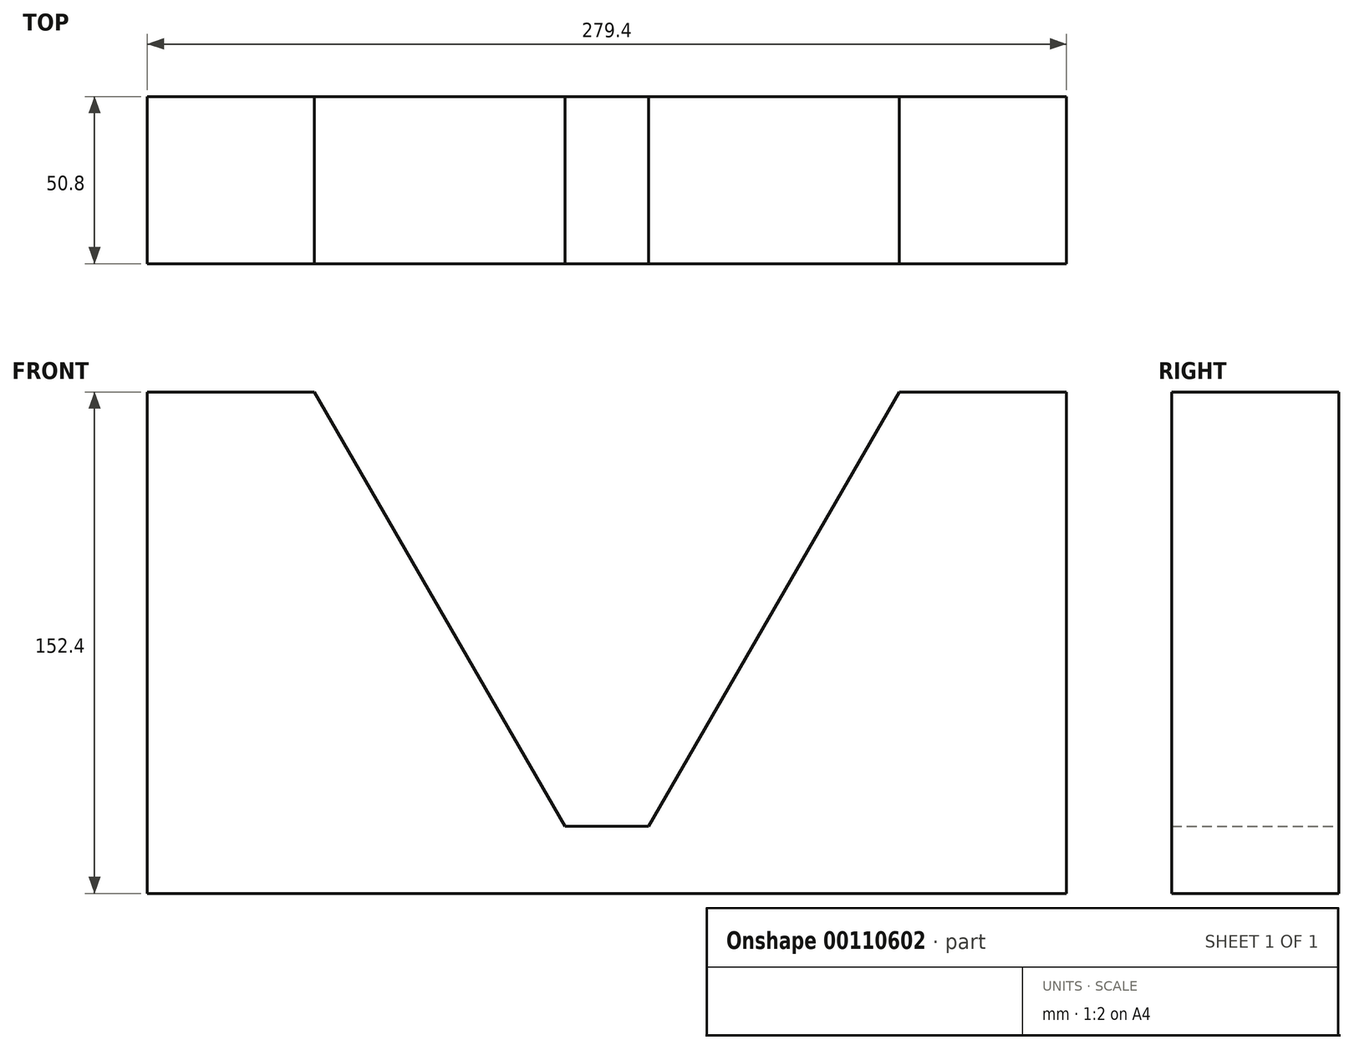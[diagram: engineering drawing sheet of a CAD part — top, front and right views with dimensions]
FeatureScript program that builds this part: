
annotation { "Feature Type Name" : "Feature", "Feature Type Description" : "" }
export const myFeature = defineFeature(function(context is Context, id is Id, definition is map)
    precondition{}
    {
        {
            var Q0;
            Q0=qCreatedBy(makeId("Front.planeOp"),FACE);
            var sketch = newSketch(context, id + "F0", { "sketchPlane" : qUnion([Q0])});
            skLineSegment(sketch, "E0", {"start": v(-131.37, -58.08) * mm, "end": v(148.03, -58.08) * mm});
            skLineSegment(sketch, "E1", {"start": v(148.03, -58.08) * mm, "end": v(148.03, 94.32) * mm});
            skLineSegment(sketch, "E2", {"start": v(148.03, 94.32) * mm, "end": v(97.23, 94.32) * mm});
            skLineSegment(sketch, "E3", {"start": v(97.23, 94.32) * mm, "end": v(21.03, -37.66) * mm});
            skLineSegment(sketch, "E4", {"start": v(21.03, -37.66) * mm, "end": v(-4.37, -37.66) * mm});
            skLineSegment(sketch, "E5", {"start": v(-131.37, -58.08) * mm, "end": v(-131.37, 94.32) * mm});
            skLineSegment(sketch, "E6", {"start": v(-131.37, 94.32) * mm, "end": v(-80.57, 94.32) * mm});
            skLineSegment(sketch, "E7", {"start": v(-80.57, 94.32) * mm, "end": v(-4.37, -37.66) * mm});
            skSolve(sketch);
        }
        {
            var Q0;
            Q0 = qSketchRegion(id + "F0", true);
            extrude(context, id + "F1", {"entities" : qUnion([Q0]), "depth" : 50.8 * mm});
        }
    });
